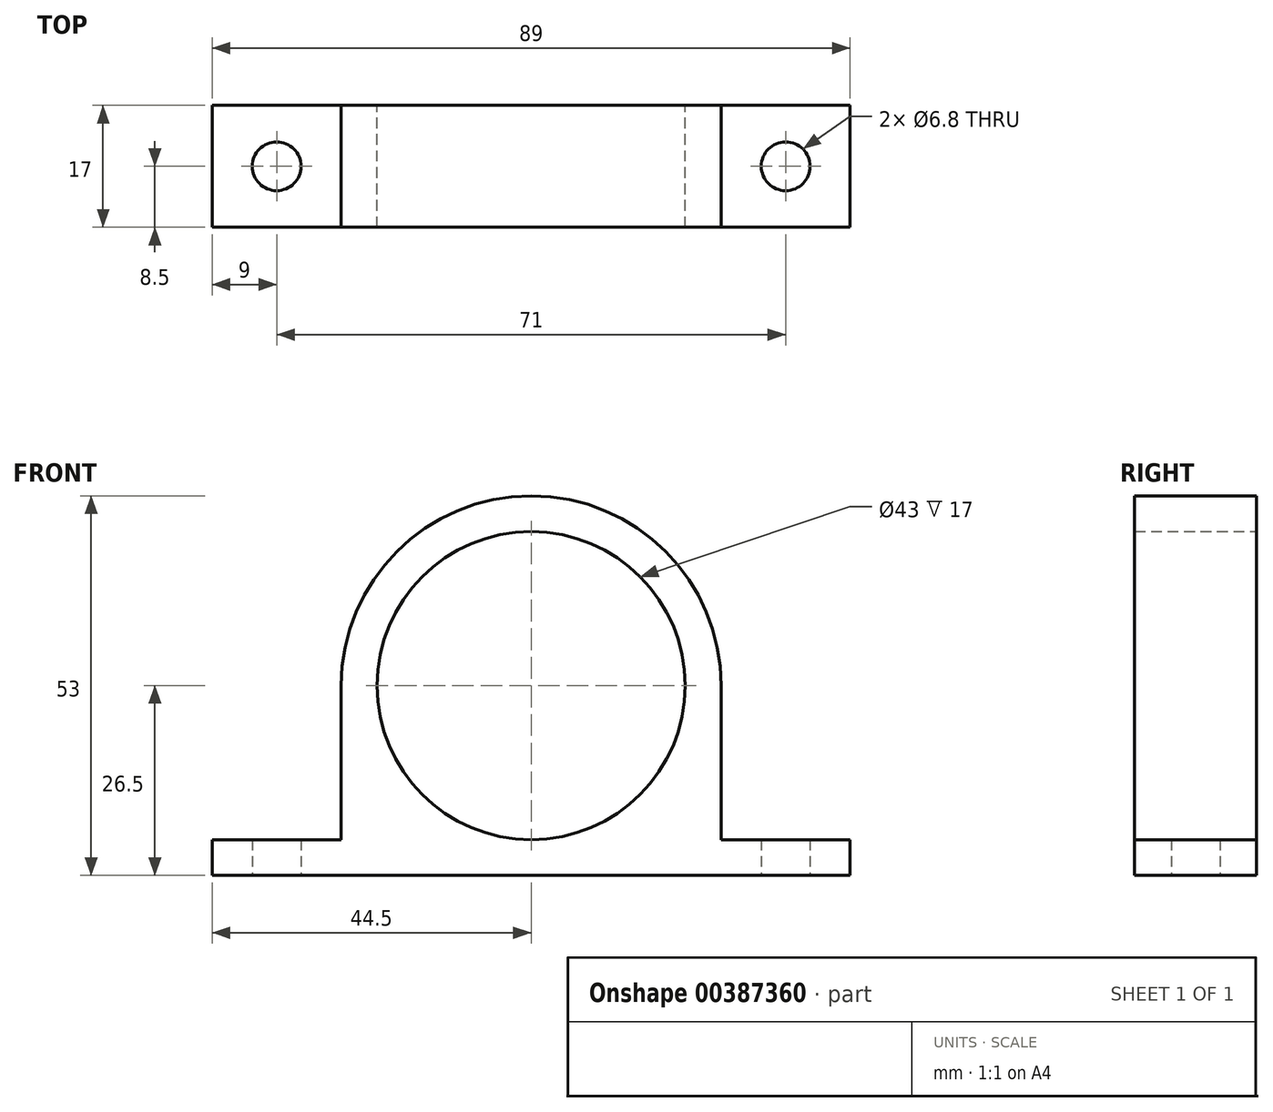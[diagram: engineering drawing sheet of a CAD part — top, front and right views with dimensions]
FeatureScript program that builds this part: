
annotation { "Feature Type Name" : "Feature", "Feature Type Description" : "" }
export const myFeature = defineFeature(function(context is Context, id is Id, definition is map)
    precondition{}
    {
        {
            var Q0;
            Q0=qCreatedBy(makeId("Front.planeOp"),FACE);
            var sketch = newSketch(context, id + "F0", { "sketchPlane" : qUnion([Q0])});
            skCircle(sketch, "E0", {"center": v(0, 0) * mm, "radius": 21.5 * mm});
            skPoint(sketch, "E1", {"position": v(-26.5, 0) * mm});
            skPoint(sketch, "E2", {"position": v(26.5, 0) * mm});
            skPoint(sketch, "E3", {"position": v(0, -26.5) * mm});
            skPoint(sketch, "E4", {"position": v(-26.5, -26.5) * mm});
            skPoint(sketch, "E5", {"position": v(26.5, -26.5) * mm});
            skLineSegment(sketch, "E6", {"start": v(-26.5, -26.5) * mm, "end": v(-35.5, -26.5) * mm, "construction": true});
            skLineSegment(sketch, "E7", {"start": v(26.5, -26.5) * mm, "end": v(35.5, -26.5) * mm, "construction": true});
            skPoint(sketch, "E8", {"position": v(-35.5, -26.5) * mm});
            skPoint(sketch, "E9", {"position": v(35.5, -26.5) * mm});
            skLineSegment(sketch, "E10", {"start": v(-26.5, -26.5) * mm, "end": v(-44.5, -26.5) * mm, "construction": true});
            skLineSegment(sketch, "E11", {"start": v(26.5, -26.5) * mm, "end": v(44.5, -26.5) * mm, "construction": true});
            skPoint(sketch, "E12", {"position": v(-44.5, -26.5) * mm});
            skPoint(sketch, "E13", {"position": v(44.5, -26.5) * mm});
            skLineSegment(sketch, "E14", {"start": v(-44.5, -26.5) * mm, "end": v(-44.5, -21.5) * mm});
            skLineSegment(sketch, "E15", {"start": v(-44.5, -26.5) * mm, "end": v(44.5, -26.5) * mm});
            skLineSegment(sketch, "E16", {"start": v(44.5, -26.5) * mm, "end": v(44.5, -21.5) * mm});
            skLineSegment(sketch, "E17", {"start": v(-26.5, 0) * mm, "end": v(-26.5, -21.5) * mm});
            skLineSegment(sketch, "E18", {"start": v(26.5, 0) * mm, "end": v(26.5, -21.5) * mm});
            skLineSegment(sketch, "E19", {"start": v(-44.5, -21.5) * mm, "end": v(-26.5, -21.5) * mm});
            skLineSegment(sketch, "E20", {"start": v(26.5, -21.5) * mm, "end": v(44.5, -21.5) * mm});
            skArc(sketch, "E21", {"start": v(-26.5, 0) * mm, "mid": v(0, 26.5) * mm, "end": v(26.5, 0) * mm});
            skSolve(sketch);
        }
        {
            var Q0;
            Q0=makeQuery(id+"F0.imprint","IMPRINT",FACE,{"disambiguationData":[TD([[makeQuery(id+"F0.imprint","IMPRINT",EDGE,{"derivedFrom":sQuery(id+"F0.wireOp",EDGE,"E0")}),-1.0]])]});
            extrude(context, id + "F1", {"entities" : qUnion([Q0]), "depth" : 17 * mm, "offsetDistance" : 25 * mm});
        }
        {
            var Q0;
            Q0=makeQuery(id+"F1.opExtrude","SWEPT_FACE",FACE,{"disambiguationData":[OSD([sQuery(id+"F0.wireOp",EDGE,"E15")])]});
            var sketch = newSketch(context, id + "F2", { "sketchPlane" : qUnion([Q0])});
            skPoint(sketch, "E22", {"position": v(-44.5, 17) * mm});
            skLineSegment(sketch, "E23", {"start": v(-44.5, 17) * mm, "end": v(-44.5, 8.5) * mm, "construction": true});
            skLineSegment(sketch, "E24", {"start": v(-44.5, 8.5) * mm, "end": v(44.5, 8.5) * mm, "construction": true});
            skLineSegment(sketch, "E25", {"start": v(-44.5, 8.5) * mm, "end": v(-35.5, 8.5) * mm, "construction": true});
            skLineSegment(sketch, "E26", {"start": v(44.5, 8.5) * mm, "end": v(35.5, 8.5) * mm, "construction": true});
            skPoint(sketch, "E27", {"position": v(-35.5, 8.5) * mm});
            skPoint(sketch, "E28", {"position": v(35.5, 8.5) * mm});
            skCircle(sketch, "E29", {"center": v(-35.5, 8.5) * mm, "radius": 3.4 * mm});
            skCircle(sketch, "E30", {"center": v(35.5, 8.5) * mm, "radius": 3.4 * mm});
            skSolve(sketch);
        }
        {
            var Q0;
            Q0=makeQuery(id+"F2.imprint","IMPRINT",FACE,{"disambiguationData":[TD([[makeQuery(id+"F2.imprint","IMPRINT",EDGE,{"derivedFrom":sQuery(id+"F2.wireOp",EDGE,"E29")}),1.0]])]});
            var Q1;
            Q1=makeQuery(id+"F2.imprint","IMPRINT",FACE,{"disambiguationData":[TD([[makeQuery(id+"F2.imprint","IMPRINT",EDGE,{"derivedFrom":sQuery(id+"F2.wireOp",EDGE,"E30")}),1.0]])]});
            extrude(context, id + "F3", {"entities" : qUnion([Q0, Q1]), "operationType" : NewBodyOperationType.REMOVE, "endBound" : BoundingType.THROUGH_ALL, "oppositeDirection" : true, "depth" : 25 * mm, "offsetDistance" : 25 * mm});
        }
    });
